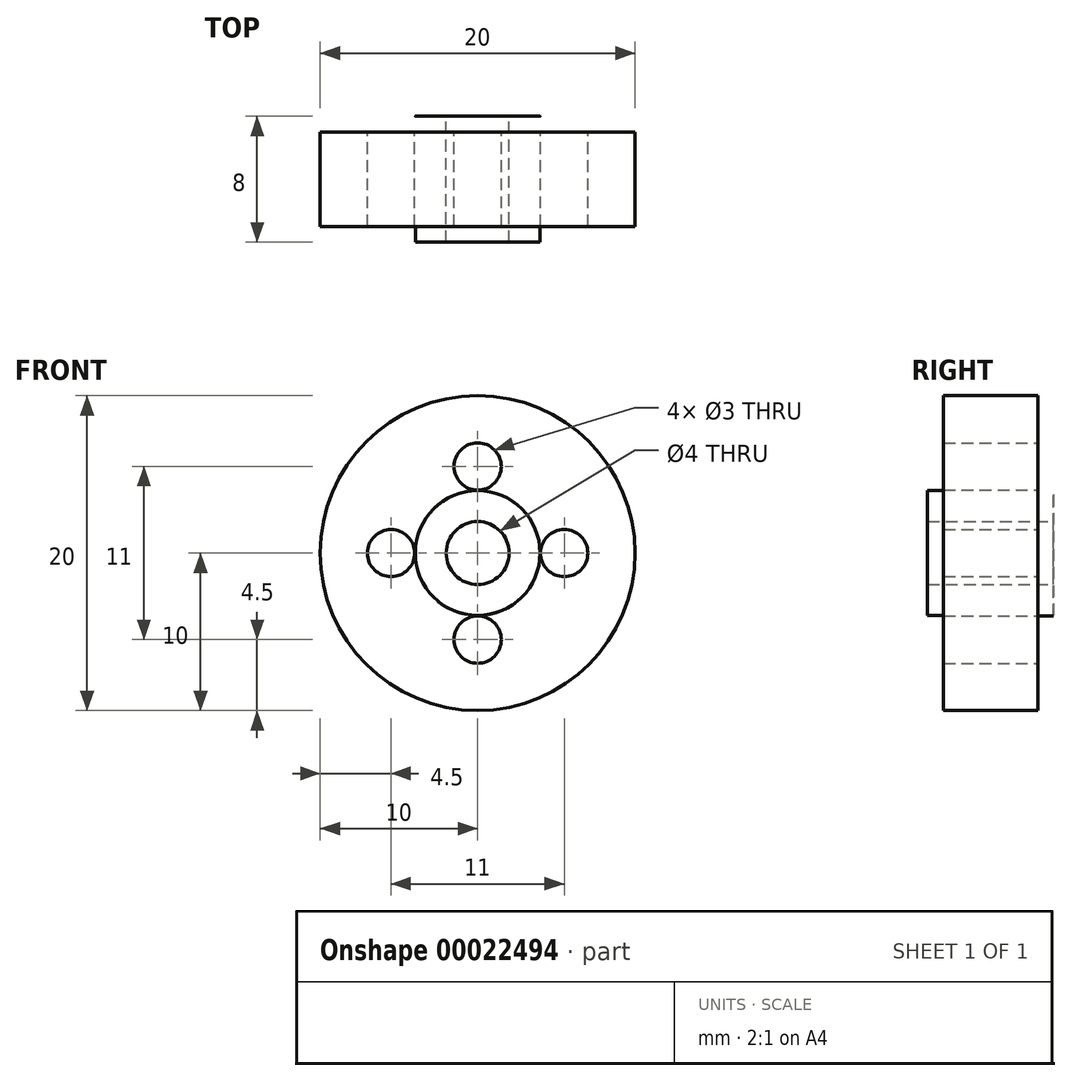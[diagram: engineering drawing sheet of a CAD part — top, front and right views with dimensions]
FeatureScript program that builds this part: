
annotation { "Feature Type Name" : "Feature", "Feature Type Description" : "" }
export const myFeature = defineFeature(function(context is Context, id is Id, definition is map)
    precondition{}
    {
        {
            var Q0;
            Q0=qCreatedBy(makeId("Front.planeOp"),FACE);
            var sketch = newSketch(context, id + "F0", { "sketchPlane" : qUnion([Q0])});
            skCircle(sketch, "E0", {"center": v(0, 0) * mm, "radius": 10 * mm});
            skPoint(sketch, "E1.center.orphan", {"position": v(0, 6.01) * mm});
            skCircle(sketch, "E2", {"center": v(0, 0) * mm, "radius": 4 * mm});
            skCircle(sketch, "E3", {"center": v(0, 0) * mm, "radius": 2 * mm});
            skCircle(sketch, "E4", {"center": v(0, 5.5) * mm, "radius": 1.5 * mm});
            skCircle(sketch, "E5.1.0", {"center": v(-5.5, 0) * mm, "radius": 1.5 * mm});
            skCircle(sketch, "E5.2.0", {"center": v(0, -5.5) * mm, "radius": 1.5 * mm});
            skCircle(sketch, "E5.3.0", {"center": v(5.5, 0) * mm, "radius": 1.5 * mm});
            skSolve(sketch);
        }
        {
            var Q0;
            Q0=makeQuery(id+"F0.imprint","IMPRINT",FACE,{"disambiguationData":[TD([[makeQuery(id+"F0.imprint","IMPRINT",EDGE,{"derivedFrom":sQuery(id+"F0.wireOp",EDGE,"E0")}),1.0]])]});
            var Q1;
            Q1=makeQuery(id+"F0.imprint","IMPRINT",FACE,{"disambiguationData":[TD([[makeQuery(id+"F0.imprint","IMPRINT",EDGE,{"derivedFrom":sQuery(id+"F0.wireOp",EDGE,"E3")}),-1.0]])]});
            extrude(context, id + "F1", {"entities" : qUnion([Q0, Q1]), "depth" : 6 * mm});
        }
        {
            var Q0;
            Q0=makeQuery(id+"F0.imprint","IMPRINT",FACE,{"disambiguationData":[TD([[makeQuery(id+"F0.imprint","IMPRINT",EDGE,{"derivedFrom":sQuery(id+"F0.wireOp",EDGE,"E3")}),-1.0]])]});
            extrude(context, id + "F2", {"entities" : qUnion([Q0]), "operationType" : NewBodyOperationType.ADD, "oppositeDirection" : true, "depth" : 1 * mm});
        }
        {
            var Q0;
            Q0=makeQuery(id+"F1.opExtrude","CAP_FACE",FACE,{"disambiguationData":[OSD([sQuery(id+"F0.wireOp",EDGE,"E0"),sQuery(id+"F0.wireOp",EDGE,"E3"),sQuery(id+"F0.wireOp",EDGE,"E4"),sQuery(id+"F0.wireOp",EDGE,"E5.1.0"),sQuery(id+"F0.wireOp",EDGE,"E5.2.0"),sQuery(id+"F0.wireOp",EDGE,"E5.3.0")])],"isStart":false});
            var sketch = newSketch(context, id + "F3", { "sketchPlane" : qUnion([Q0])});
            skCircle(sketch, "E6", {"center": v(0, 0) * mm, "radius": 3.96 * mm});
            skSolve(sketch);
        }
        {
            var Q0;
            Q0=makeQuery(id+"F3.imprint","IMPRINT",FACE,{"disambiguationData":[TD([[makeQuery(id+"F3.imprint","IMPRINT",EDGE,{"derivedFrom":makeQuery(id+"F1.opExtrude","CAP_EDGE",EDGE,{"disambiguationData":[OSD([sQuery(id+"F0.wireOp",EDGE,"E3")])],"isStart":false})}),-1.0]])]});
            extrude(context, id + "F4", {"entities" : qUnion([Q0]), "operationType" : NewBodyOperationType.ADD, "depth" : 1 * mm});
        }
    });
